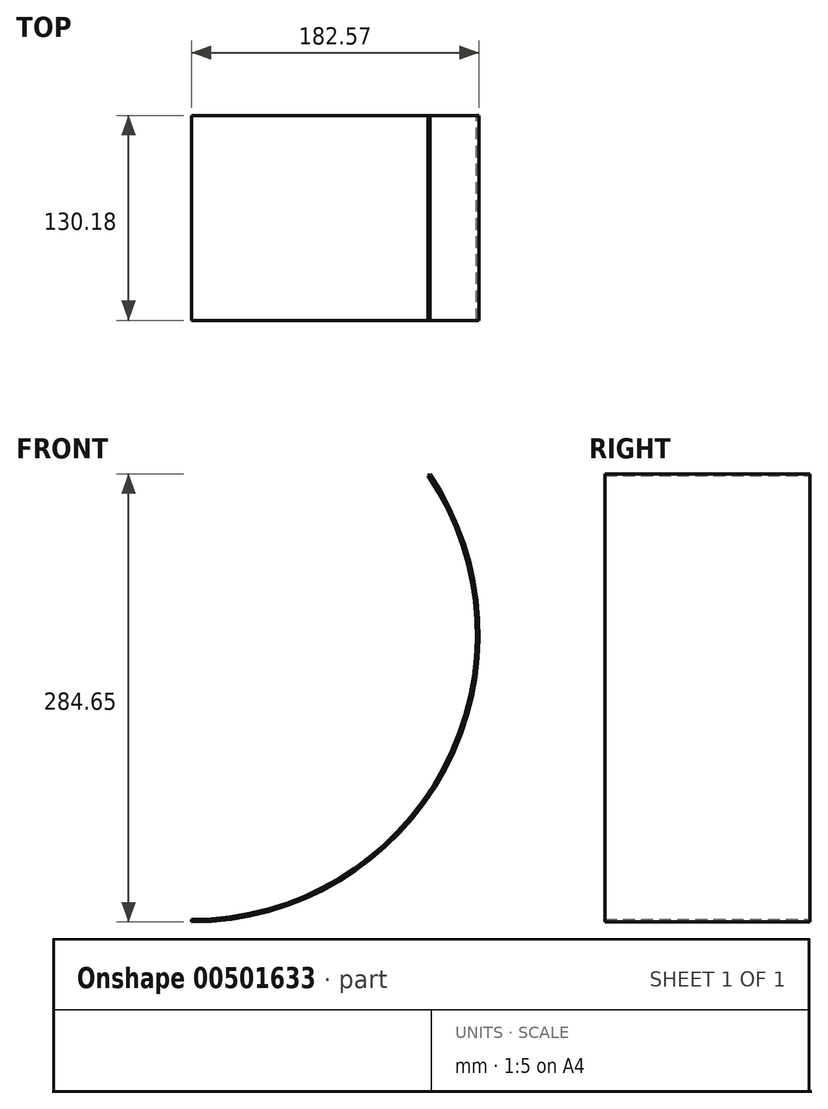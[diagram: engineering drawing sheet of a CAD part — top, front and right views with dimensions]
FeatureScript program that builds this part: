
annotation { "Feature Type Name" : "Feature", "Feature Type Description" : "" }
export const myFeature = defineFeature(function(context is Context, id is Id, definition is map)
    precondition{}
    {
        {
            var Q0;
            Q0=qCreatedBy(makeId("Front.planeOp"),FACE);
            var sketch = newSketch(context, id + "F0", { "sketchPlane" : qUnion([Q0])});
            skArc(sketch, "E0", {"start": v(-151.95, -108.13) * mm, "mid": v(9.25, -11.28) * mm, "end": v(-0.6, 176.52) * mm});
            skCircle(sketch, "E1", {"center": v(-151.95, 74.43) * mm, "radius": 61.91 * mm, "construction": true});
            skLineSegment(sketch, "E2", {"start": v(-151.95, 74.43) * mm, "end": v(-151.95, -224.4) * mm, "construction": true});
            skLineSegment(sketch, "E3", {"start": v(-151.95, -108.13) * mm, "end": v(75.6, -108.13) * mm});
            skLineSegment(sketch, "E4", {"start": v(75.6, -108.13) * mm, "end": v(75.6, 176.52) * mm});
            skLineSegment(sketch, "E5", {"start": v(75.6, 176.52) * mm, "end": v(-0.6, 176.52) * mm});
            skLineSegment(sketch, "E6", {"start": v(-151.95, 74.43) * mm, "end": v(225.65, 74.43) * mm, "construction": true});
            skLineSegment(sketch, "E7", {"start": v(30.62, 74.43) * mm, "end": v(-0.6, 176.52) * mm, "construction": true});
            skLineSegment(sketch, "E8", {"start": v(30.62, 74.43) * mm, "end": v(30.62, 328.43) * mm, "construction": true});
            skCircle(sketch, "E9", {"center": v(21.43, 157.13) * mm, "radius": 3.18 * mm, "construction": true});
            skCircle(sketch, "E10.1.0", {"center": v(39.61, 88.67) * mm, "radius": 3.18 * mm, "construction": true});
            skCircle(sketch, "E10.2.0", {"center": v(31.75, 18.27) * mm, "radius": 3.18 * mm, "construction": true});
            skCircle(sketch, "E10.3.0", {"center": v(-1.1, -44.49) * mm, "radius": 3.18 * mm, "construction": true});
            skCircle(sketch, "E10.4.0", {"center": v(-54.46, -91.08) * mm, "radius": 3.18 * mm, "construction": true});
            skLineSegment(sketch, "E10.anchor1", {"start": v(-151.95, 74.43) * mm, "end": v(21.43, 157.13) * mm, "construction": true});
            skLineSegment(sketch, "E10.anchor2", {"start": v(-151.95, 74.43) * mm, "end": v(-54.46, -91.08) * mm, "construction": true});
            skArc(sketch, "E11.0", {"start": v(-151.95, -106.54) * mm, "mid": v(7.84, -10.53) * mm, "end": v(-1.91, 175.63) * mm});
            skLineSegment(sketch, "E12", {"start": v(-0.6, 176.52) * mm, "end": v(-1.91, 175.63) * mm});
            skLineSegment(sketch, "E13", {"start": v(-151.95, -106.54) * mm, "end": v(-151.95, -108.13) * mm});
            skSolve(sketch);
        }
        {
            var Q0;
            Q0=makeQuery(id+"F0.imprint","IMPRINT",FACE,{"disambiguationData":[TD([[makeQuery(id+"F0.imprint","IMPRINT",EDGE,{"derivedFrom":sQuery(id+"F0.wireOp",EDGE,"E0")}),1.0]])]});
            extrude(context, id + "F1", {"entities" : qUnion([Q0]), "depth" : 130.17 * mm});
        }
    });
